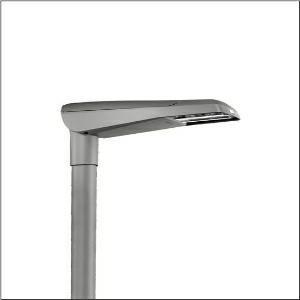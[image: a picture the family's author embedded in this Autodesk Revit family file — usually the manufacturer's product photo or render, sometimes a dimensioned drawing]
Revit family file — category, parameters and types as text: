
# Revit family: streetlight_sl_11_iq_micro___st1_2a_5xc1ac1f08ce_6c95
name_source: partatom
category: Lighting Fixtures
units: mm (PartAtom-declared; Revit-internal decimal feet)

## family parameters
Cut with Voids When Loaded = No
Host = Face
Light Source = No
Part Type = Normal
Room Calculation Point = No
Round Connector Dimension = Use Diameter
Shared = No

## types (1)
- --- (1 x LED, 1600 lm, 14 W, 2200K)
    Apparent Load = 14 VA
    CIE Flux Codes = 33 71 96 100 100
    Color Rendering = 70
    Color Temperature = 2200K
    Default Elevation = 1800 mm
    Description = Streetlight SL 11 iQ micro, mast luminaire, primary light control with 3 zone facetted reflector, of plastic, silver coated, highly specular, primary optical cover: cover, of PMMA, transparent, light distribution: ST1.2a, light emission: direct distribution, primary light characteristic: asymmetric, installation type: post-top, side-entry, lamps: LED, High Power LED, rated values: 1.880lm | 13,8W | 136,2lm/W (begin service life); end service life: 1.880lm | 14W; at 50% lumin. flux: 940lm | 7,5W | 125,3lm/W, colour temperature: 2200/2700/3000/4000K, colour rendering: CRI > 70, light colour: 722/727/730/740, light setting 1 begin service life: 100% | 1.880lm | 13,8W | 136,2lm/W | 3.000K, light setting 1 end service life: 14W, further light settings possible, control: Street-Remote, Auto-Match, Temp-Guard, Lumen-Switch, Night-Set, Smart-Wire, Light-Fading, Desk-Remote (wireless, voltage-free reading and setting of iQ features in the workshop via application-optimized NFC function/RFID function), optimised constant luminous flux control (CLO 2.0), with cable H07RN-F 5x 1.5mm², mains connection: 220..240V, AC, 50/60Hz, connection cable pre-assembled, cable length: 5,5m, luminaire housing, of diecast aluminium, powder-coated, Siteco® metallic grey (DB 702S), please order mast flange separately, inclination adjustable without tools: 0°, 5°, 10°, 15° (post-top) | 0°, -5°, -10°, -15° (side-entry), sealing non-destructively replaceable, multi-level sealing system, length: 600mm, width: 174mm, height: 116mm, mast flange for spigot size: 42mm (side-entry): 5XC10008XM4, 60/48mm (side-entry/post-top): 5XC10108XM2, 76/60mm (side-entry/post-top): 5XC10108XM1, equipment: standard, protection rating (complete): IP66, insulation class (complete): insulation class II (safety insulation), certification: CE, ENEC, ENEC+, VDE, impact resistance: IK10, permissible operating ambient temperature for outdoor applications: -25..+50°C, standard-compliant lighting for roads and squares, Environmental Product Declaration (EPD) tested and certified by an independent institute, packaging unit: 1 piece

Light Distribution: ST1.2a
    Height = 116 mm
    Lamp = 1 x LED
    Lamp Light Flux = 1600 lm
    Lamp Power = 14 W
    Lamp count = 1
    Length = 600 mm
    Luminous efficacy = 114 lm/W
    Manufacturer = Siteco
    ModVariant = No
    Model = 5XC1AC1F08CE
    Number of Poles = 1
    OnlyDefault = Yes
    Power Factor = 1
    Product Name = Streetlight SL 11 iQ micro | ST1.2a
    Product group = mast luminaire | pylon top
    ProductGroupID = 6100
    Protection Class = Protection class II
    Protection Degree = IP 66
    RLX_Detail_Level = 1
    RLX_Emergency_Light_Flux = 0 lm
    RLX_Emergency_Type = 0
    RLX_Emergency_Type_DB = No
    RlxData = <blob elided: 58373 chars, md5=c73ce1ad>
    Socket = socket
    Standby Power = 0 W
    System Light Flux = 1600 lm
    System Power = 14 W
    Type Comments = individual setting: luminous flux: 100 % | dim-lin: 254 | 369 mA
    Type Image = l_1006566.jpg
    URL = http://relux.com
    VarID = @adj_055665
    Voltage = 0 V
    Weight = 0.00 kg
    Width = 174 mm

## geometry (parser evidence)
native form markers: Blend x4, Sweep x11
no freeform markers — native parametric forms only
